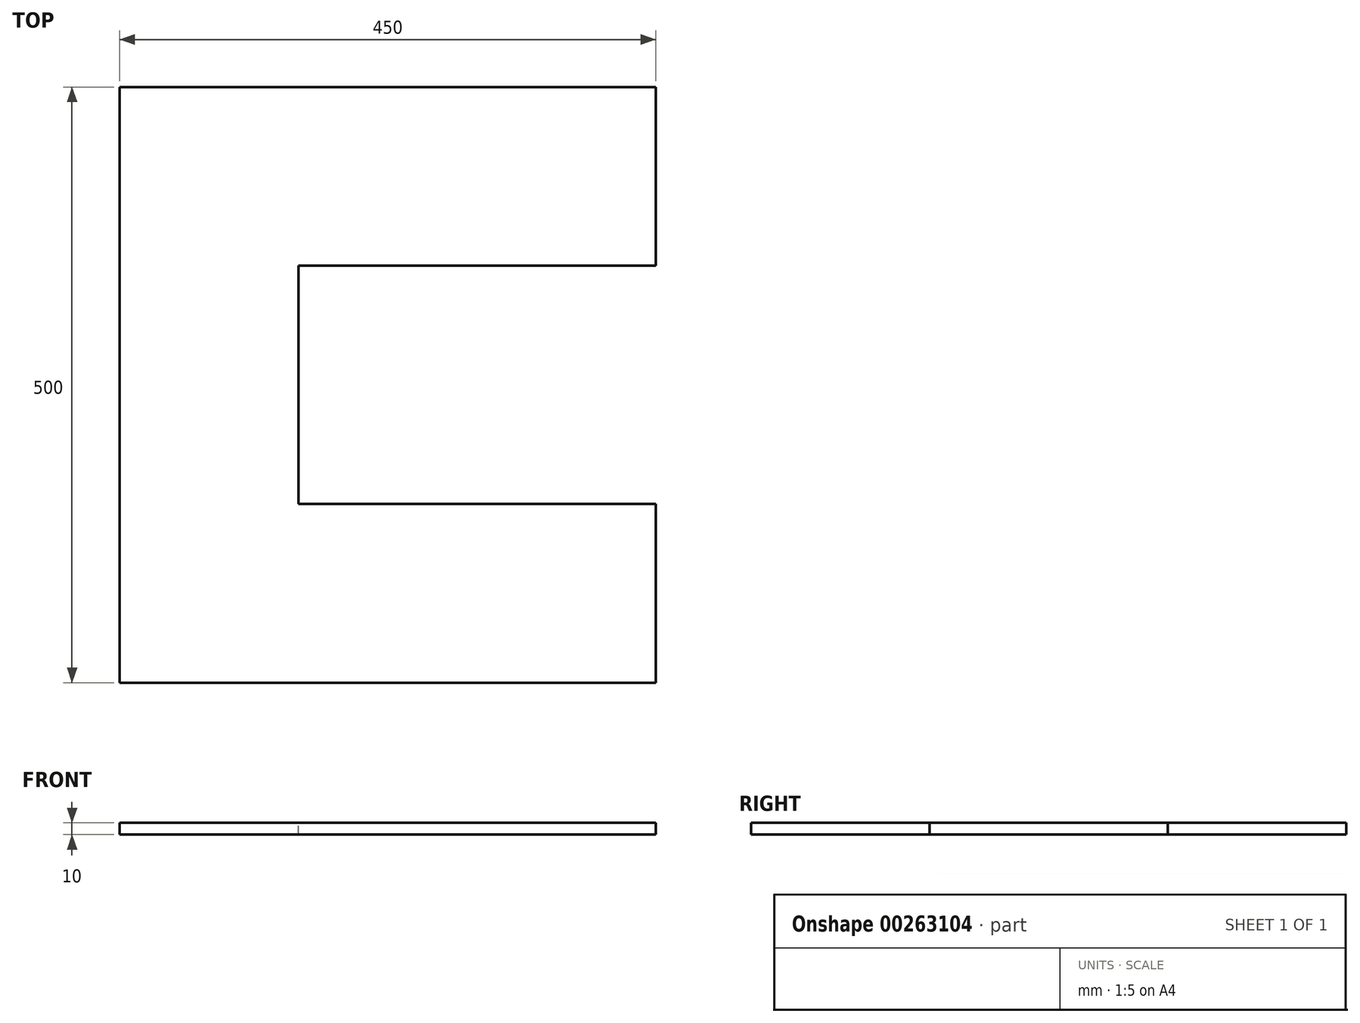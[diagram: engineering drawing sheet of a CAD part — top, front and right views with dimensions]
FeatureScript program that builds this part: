
annotation { "Feature Type Name" : "Feature", "Feature Type Description" : "" }
export const myFeature = defineFeature(function(context is Context, id is Id, definition is map)
    precondition{}
    {
        {
            var Q0;
            Q0=qCreatedBy(makeId("Top.planeOp"),FACE);
            var sketch = newSketch(context, id + "F0", { "sketchPlane" : qUnion([Q0])});
            skLineSegment(sketch, "E0.bottom", {"start": v(225, -250) * mm, "end": v(-225, -250) * mm});
            skLineSegment(sketch, "E0.top", {"start": v(225, 250) * mm, "end": v(-225, 250) * mm});
            skLineSegment(sketch, "E0.left", {"start": v(225, -250) * mm, "end": v(225, 250) * mm});
            skLineSegment(sketch, "E0.right", {"start": v(-225, -250) * mm, "end": v(-225, 250) * mm});
            skPoint(sketch, "E0.middle", {"position": v(0, 0) * mm});
            skSolve(sketch);
        }
        {
            var Q0;
            Q0 = qSketchRegion(id + "F0", true);
            extrude(context, id + "F1", {"entities" : qUnion([Q0]), "depth" : 10 * mm});
        }
        {
            var Q0;
            Q0=makeQuery(id+"F1.opExtrude","CAP_FACE",FACE,{"disambiguationData":[OSD([sQuery(id+"F0.wireOp",EDGE,"E0.bottom"),sQuery(id+"F0.wireOp",EDGE,"E0.top"),sQuery(id+"F0.wireOp",EDGE,"E0.left"),sQuery(id+"F0.wireOp",EDGE,"E0.right")])],"isStart":false});
            var sketch = newSketch(context, id + "F2", { "sketchPlane" : qUnion([Q0])});
            skLineSegment(sketch, "E1.bottom", {"start": v(225, -100) * mm, "end": v(-75, -100) * mm});
            skLineSegment(sketch, "E1.top", {"start": v(225, 100) * mm, "end": v(-75, 100) * mm});
            skLineSegment(sketch, "E1.left", {"start": v(225, -100) * mm, "end": v(225, 100) * mm});
            skLineSegment(sketch, "E1.right", {"start": v(-75, -100) * mm, "end": v(-75, 100) * mm});
            skSolve(sketch);
        }
        {
            var Q0;
            Q0 = qSketchRegion(id + "F2", true);
            extrude(context, id + "F3", {"entities" : qUnion([Q0]), "operationType" : NewBodyOperationType.REMOVE, "oppositeDirection" : true, "depth" : 10 * mm});
        }
    });
